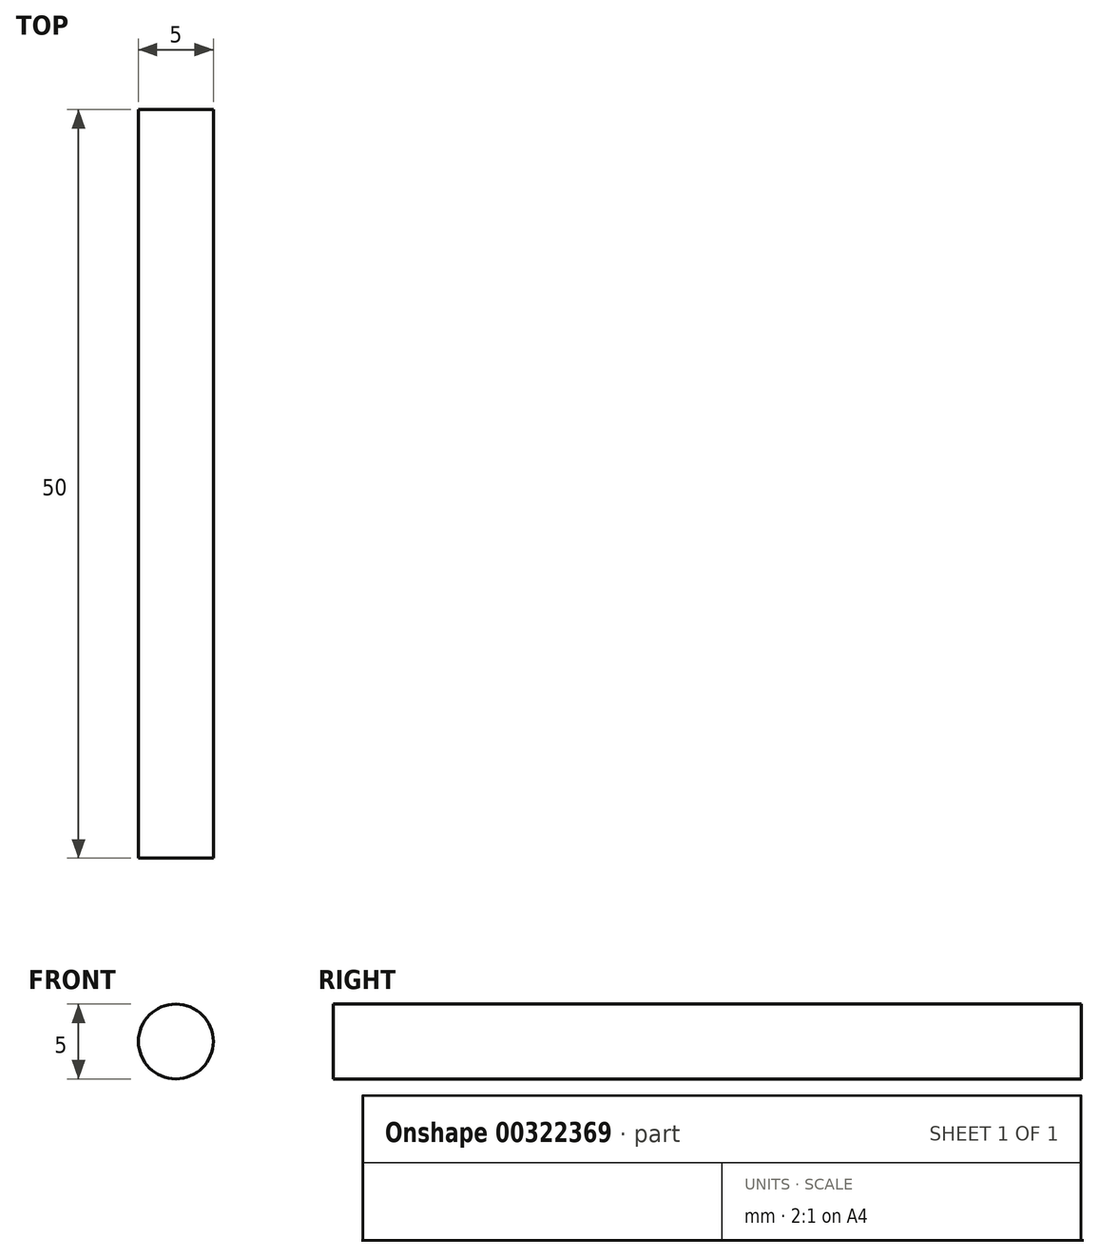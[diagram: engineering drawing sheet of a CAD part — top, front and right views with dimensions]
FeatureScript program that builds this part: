
annotation { "Feature Type Name" : "Feature", "Feature Type Description" : "" }
export const myFeature = defineFeature(function(context is Context, id is Id, definition is map)
    precondition{}
    {
        {
            var Q0;
            Q0=qCreatedBy(makeId("Front.planeOp"),FACE);
            var sketch = newSketch(context, id + "F0", { "sketchPlane" : qUnion([Q0])});
            skCircle(sketch, "E0", {"center": v(0, 0) * mm, "radius": 2.5 * mm});
            skSolve(sketch);
        }
        {
            var Q0;
            Q0=qSketchRegion(id+"F0",true);
            extrude(context, id + "F1", {"entities" : qUnion([Q0]), "endBound" : BoundingType.SYMMETRIC, "depth" : 50 * mm});
        }
    });
